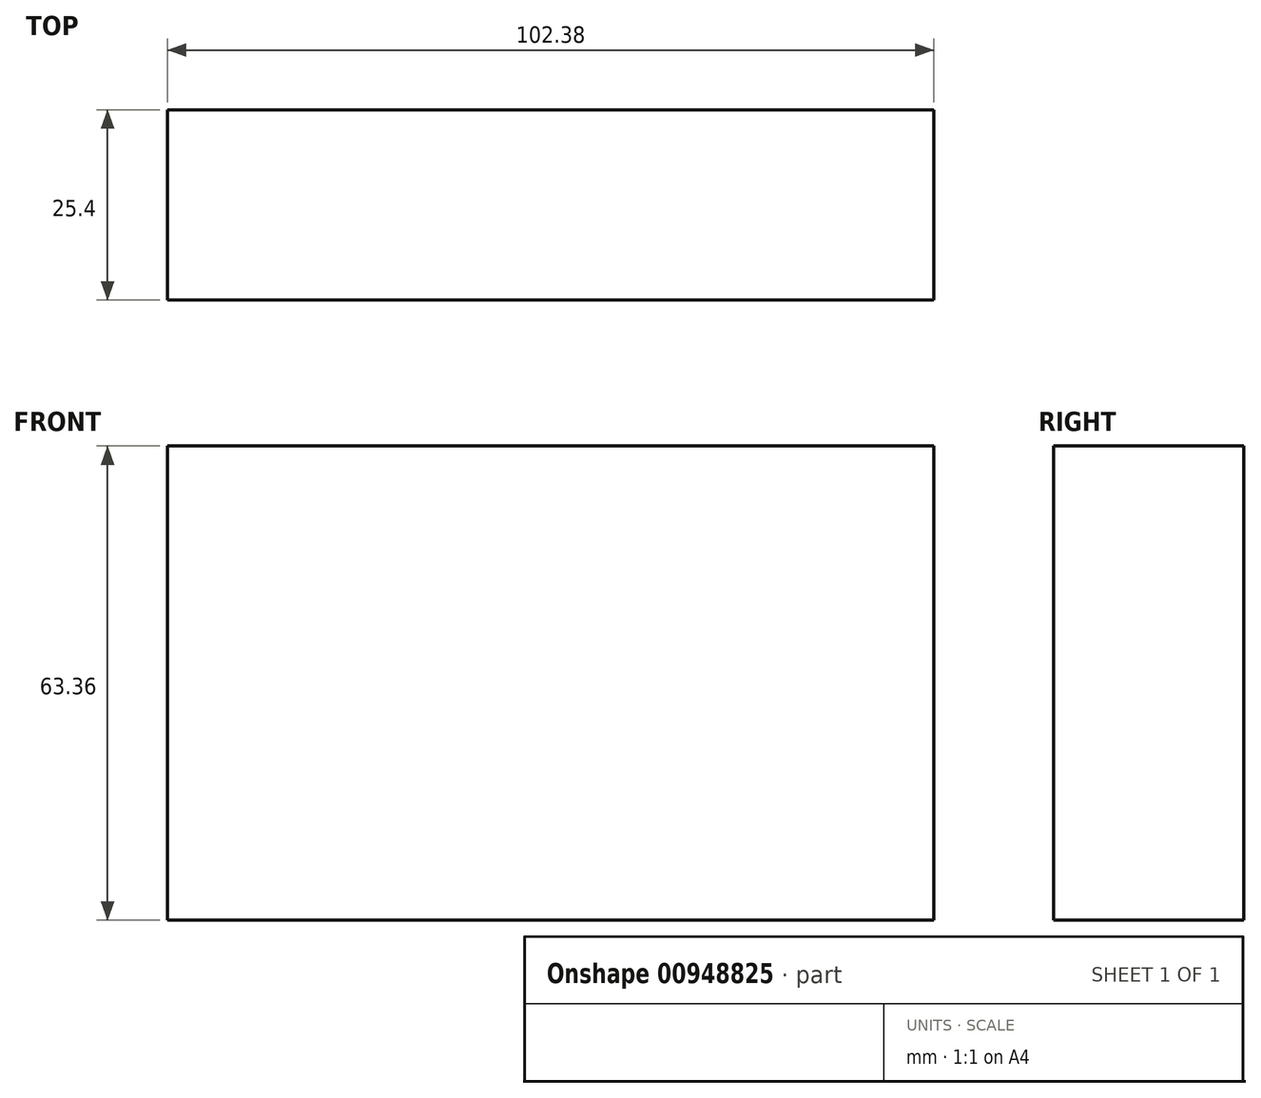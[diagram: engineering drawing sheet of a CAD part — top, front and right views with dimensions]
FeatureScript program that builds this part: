
annotation { "Feature Type Name" : "Feature", "Feature Type Description" : "" }
export const myFeature = defineFeature(function(context is Context, id is Id, definition is map)
    precondition{}
    {
        {
            var Q0;
            Q0=qCreatedBy(makeId("Front.planeOp"),FACE);
            var sketch = newSketch(context, id + "F0", { "sketchPlane" : qUnion([Q0])});
            skLineSegment(sketch, "E0.bottom", {"start": v(-52.6, 36.36) * mm, "end": v(49.78, 36.36) * mm});
            skLineSegment(sketch, "E0.top", {"start": v(-52.6, -27) * mm, "end": v(49.78, -27) * mm});
            skLineSegment(sketch, "E0.left", {"start": v(-52.6, 36.36) * mm, "end": v(-52.6, -27) * mm});
            skLineSegment(sketch, "E0.right", {"start": v(49.78, 36.36) * mm, "end": v(49.78, -27) * mm});
            skSolve(sketch);
        }
        {
            var Q0;
            Q0=makeQuery(id+"F0.imprint","IMPRINT",FACE,{"disambiguationData":[TD([[makeQuery(id+"F0.imprint","IMPRINT",EDGE,{"derivedFrom":sQuery(id+"F0.wireOp",EDGE,"E0.bottom")}),-1.0]])]});
            extrude(context, id + "F1", {"entities" : qUnion([Q0]), "depth" : 25.4 * mm, "offsetDistance" : 25.4 * mm});
        }
    });
